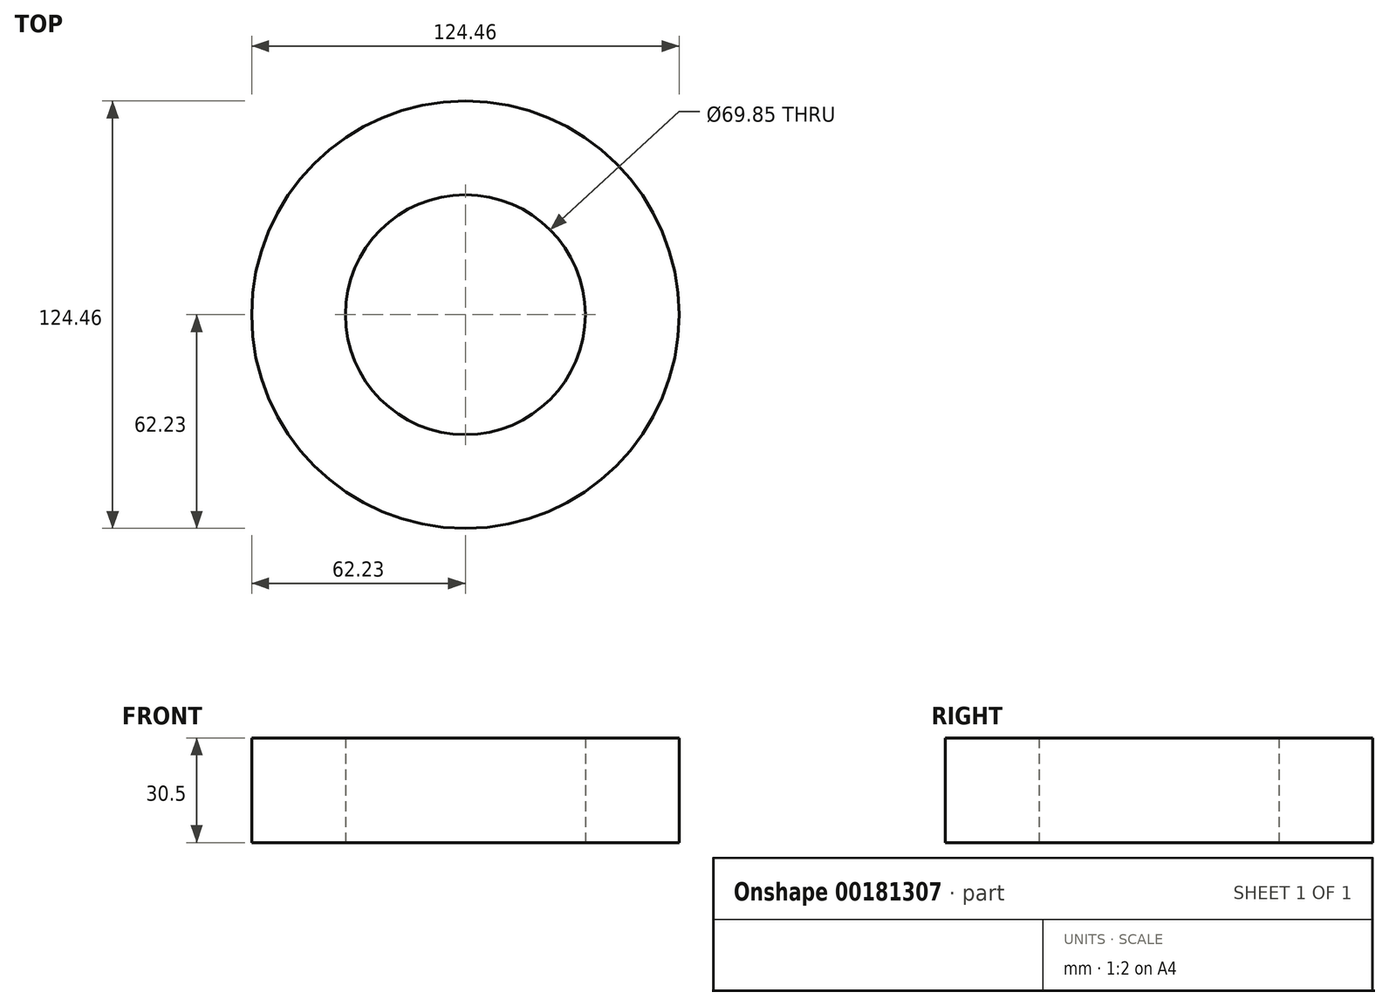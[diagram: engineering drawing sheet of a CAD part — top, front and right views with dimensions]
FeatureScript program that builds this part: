
annotation { "Feature Type Name" : "Feature", "Feature Type Description" : "" }
export const myFeature = defineFeature(function(context is Context, id is Id, definition is map)
    precondition{}
    {
        {
            var Q0;
            Q0=qCreatedBy(makeId("Top.planeOp"),FACE);
            var sketch = newSketch(context, id + "F0", { "sketchPlane" : qUnion([Q0])});
            skCircle(sketch, "E0", {"center": v(0, 0) * mm, "radius": 62.23 * mm});
            skCircle(sketch, "E1", {"center": v(0, 0) * mm, "radius": 34.93 * mm});
            skSolve(sketch);
        }
        {
            var Q0;
            Q0 = qSketchRegion(id + "F0", true);
            extrude(context, id + "F1", {"entities" : qUnion([Q0]), "depth" : 30.5 * mm});
        }
    });
